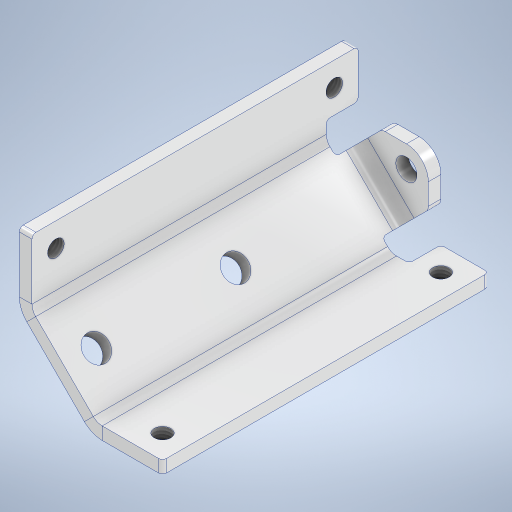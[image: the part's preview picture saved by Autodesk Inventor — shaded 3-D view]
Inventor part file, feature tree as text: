
AUTODESK INVENTOR PART (.ipt)
format: ipt  version: 2024 (Build 280153000, 153)  size: 444,928 bytes
history: native  units: mm
features: sketch x9, sheet_metal_op x8, projected_geometry x8, hole x4, other x3, extrude x2, fillet x2
ambient origin geometry x8: Origin, YZ Plane, XZ Plane, XY Plane, X Axis, Y Axis, Z Axis, Center Point
bodies: Solid1 (feature_tree)
feature tree (36):
  sheet_metal_op  "Contour Flange1"
  sketch  "Sketch4"  dims[d2=3.0mm d4=31.5mm]
  hole  "Hole1"  [1 undecoded]
  sketch  "Sketch5"  dims[d5=31.5mm d6=24.0mm d7=7.5mm]
  hole  "Hole2"  [1 undecoded]
  extrude  "Extrusion3"  Depth=24.0mm
  fillet  "Fillet1"  Radius=7.5mm
  sketch  "Sketch9"  dims[d24=82.0mm]
  sheet_metal_op  "Face3"
  sheet_metal_op  "Flange1"
  hole  "Hole3"  [1 undecoded]
  sketch  "Sketch11"  dims[d26=3.175mm d27=12.7mm d28=3.175mm d29=3.175mm d30=4.134mm d31=10.0mm d32=4.0mm d33=2.0mm d34=90.0deg d35=3.175mm d36=20.594885mm d39=4.134mm d40=10.0mm d41=4.0mm d42=2.0mm d43=90.0deg d44=8.0mm d45=20.594885mm d48=2.0mm d49=2.0mm d50=2.0mm d52=8.0mm d53=0.0mm d54=1.0mm d55=6.0mm d56=6.0mm d57=3.175mm d58=1.5875mm d59=6.35mm d60=3.175mm d61=14.5mm d62=90.0deg d63=3.175mm d64=12.7mm d65=3.175mm d66=3.175mm d67=35.0mm d68=8.0mm d69=6.3mm d70=10.0mm d71=4.0mm d72=2.0mm d73=90.0deg d74=8.0mm d75=20.594885mm d76=70.0mm d77=1.0mm d78=3.175mm d79=3.175mm d80=1.5875mm d81=6.35mm d82=3.175mm d83=11.0mm d84=0.0mm d85=0.0mm d86=2.0mm d87=5.3mm d88=12.0mm d89=4.0mm d90=2.0mm d91=90.0deg d92=8.0mm d93=20.594885mm d94=17.5mm]
  extrude  "Extrusion4"  Depth=3.175mm
  fillet  "Fillet2"  Radius=1.5875mm
  hole  "Hole4"  [1 undecoded]
  sketch  "Sketch1"  dims[d0=30.0mm d1=3.0mm]
  other  "Plate3"
  sheet_metal_op  "Bend2"
  sheet_metal_op  "Corner1"
  projected_geometry  "Projected Loop1"
  projected_geometry  "Projected Loop2"
  sketch  "Sketch6"  dims[d10=3.175mm d18=6.0mm]
  projected_geometry  "Projected Loop3"
  projected_geometry  "Projected Loop4"
  projected_geometry  "Projected Loop5"
  projected_geometry  "Projected Loop6"
  projected_geometry  "Projected Loop7"
  sketch  "Sketch7"  dims[d19=6.0mm d20=3.175mm d21=1.5875mm]
  other  "Plate4"
  sheet_metal_op  "Bend3"
  sheet_metal_op  "Corner2"
  sketch  "Sketch8"  dims[d22=6.35mm d23=3.175mm]
  sketch  "Sketch10"  dims[d25=3.175mm]
  other  "Plate5"
  sheet_metal_op  "Bend4"
  projected_geometry  "Projected Loop8"
note: 4 required parameter values undecoded (feature->parameter linkage not recoverable at this tier; creation-order binding heuristic only, values carry confidence <= 0.55)
